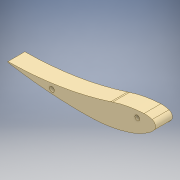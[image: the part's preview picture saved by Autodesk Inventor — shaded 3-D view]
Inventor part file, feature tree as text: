
AUTODESK INVENTOR PART (.ipt)
format: ipt  version: 2018 (Build 220112000, 112)  size: 113,152 bytes
history: native  units: mm
features: extrude x1, sketch x1, projected_geometry x1
ambient origin geometry x8: Origin, YZ Plane, XZ Plane, XY Plane, X Axis, Y Axis, Z Axis, Center Point
bodies: Body1 (feature_tree)
feature tree (3):
  extrude  "押し出し1"  Depth=41.5mm TaperAngle=0.0deg
  sketch  "スケッチ1"
  projected_geometry  "投影ループ1"
